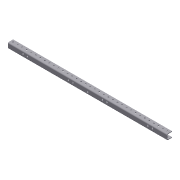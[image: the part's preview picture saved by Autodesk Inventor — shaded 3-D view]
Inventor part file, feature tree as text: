
AUTODESK INVENTOR PART (.ipt)
format: ipt  version: 2011 (Build 150239000, 239)  size: 320,512 bytes
history: native  units: in
note: dims shown in document units (in); Inventor stores cm internally (conversion verified against a paired STEP export)
features: sheet_metal_op x6, sketch x5, projected_geometry x4, other x3, hole x2, pattern_linear x1, plane x1
ambient origin geometry x8: Origin, YZ Plane, XZ Plane, XY Plane, X Axis, Y Axis, Z Axis, Center Point
feature tree (22):
  sheet_metal_op  "Face2"
  sheet_metal_op  "Flange1"
  sheet_metal_op  "Unfold1"
  hole  "Hole1"  [1 undecoded]
  pattern_linear  "Rectangular Pattern1"  Spacing1=0.25in  [1 undecoded]
  hole  "Hole2"  [1 undecoded]
  sheet_metal_op  "Refold1"
  plane  "Work Plane1"
  sketch  "Sketch3"  dims[d4=0.75in]
  other  "Plate2"
  sketch  "Sketch4"  dims[d5=0.125in]
  other  "Plate3"
  sheet_metal_op  "Bend1"
  sheet_metal_op  "Corner1"
  sketch  "Sketch6"  dims[d6=0.125in]
  projected_geometry  "Projected Loop1"
  projected_geometry  "Projected Loop2"
  projected_geometry  "Projected Loop3"
  projected_geometry  "Projected Loop4"
  sketch  "Sketch7"  dims[d7=0.0625in d8=0.25in d9=0.125in d10=1.125in d11=90.0deg d12=0.125in d13=0.5in d14=0.125in d15=0.125in d19=0.5in d20=0.5in d21=0.5in d22=0.5in d23=0.257in d24=0.75in d25=0.375in d26=0.25in d27=0.5635in d28=0.125in d29=0.8108in d30=13.7795in d32=1.0in d33=3.25in d34=4.25in d35=13.25in d36=14.25in d37=1.458in d38=1.608in d39=0.38in d40=0.75in d41=0.375in d42=0.25in d43=0.5635in d44=0.125in d45=0.8108in]
  other  "Definition1"
  sketch  "Sketch1"  dims[d2=0.125in d3=35.0in]
note: 3 required parameter values undecoded (feature->parameter linkage not recoverable at this tier; creation-order binding heuristic only, values carry confidence <= 0.55)
